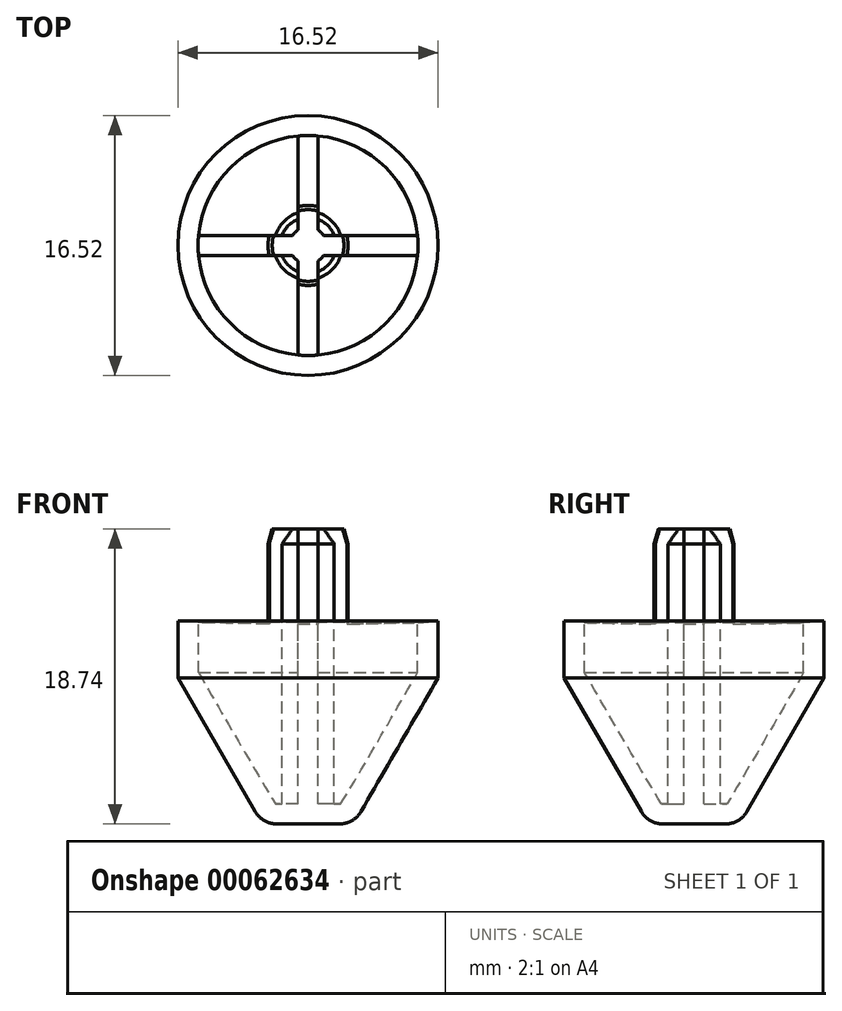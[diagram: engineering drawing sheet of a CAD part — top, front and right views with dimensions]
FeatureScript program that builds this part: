
annotation { "Feature Type Name" : "Feature", "Feature Type Description" : "" }
export const myFeature = defineFeature(function(context is Context, id is Id, definition is map)
    precondition{}
    {
        {
            var Q0;
            Q0=qCreatedBy(makeId("Front.planeOp"),FACE);
            var sketch = newSketch(context, id + "F0", { "sketchPlane" : qUnion([Q0])});
            skLineSegment(sketch, "E0.bottom", {"start": v(-2.54, 19.12) * mm, "end": v(2.54, 19.12) * mm});
            skLineSegment(sketch, "E0.top", {"start": v(-2.54, 15.94) * mm, "end": v(2.54, 15.94) * mm});
            skLineSegment(sketch, "E0.left", {"start": v(-2.54, 19.12) * mm, "end": v(-2.54, 15.94) * mm});
            skLineSegment(sketch, "E0.right", {"start": v(2.54, 19.12) * mm, "end": v(2.54, 15.94) * mm});
            skCircle(sketch, "E1", {"center": v(0, 10.12) * mm, "radius": 6.35 * mm, "construction": true});
            skLineSegment(sketch, "E2", {"start": v(0, 10.12) * mm, "end": v(0, 19.12) * mm, "construction": true});
            skLineSegment(sketch, "E3", {"start": v(-2.54, 15.94) * mm, "end": v(-8.26, 16.14) * mm});
            skLineSegment(sketch, "E4", {"start": v(0, 10.12) * mm, "end": v(0, 3.24) * mm, "construction": true});
            skLineSegment(sketch, "E5", {"start": v(-8.26, 16.14) * mm, "end": v(-8.26, 12.52) * mm});
            skLineSegment(sketch, "E6", {"start": v(-8.26, 12.52) * mm, "end": v(-2.9, 3.24) * mm});
            skLineSegment(sketch, "E7", {"start": v(-2.9, 3.24) * mm, "end": v(0, 3.24) * mm});
            skLineSegment(sketch, "E8", {"start": v(2.41, 20.39) * mm, "end": v(-2.41, 20.39) * mm});
            skLineSegment(sketch, "E9", {"start": v(0, 19.12) * mm, "end": v(0, 20.39) * mm});
            skArc(sketch, "E10", {"start": v(-2.41, 20.39) * mm, "mid": v(-2.62, 19.77) * mm, "end": v(-2.54, 19.12) * mm});
            skArc(sketch, "E11", {"start": v(2.54, 19.12) * mm, "mid": v(2.62, 19.77) * mm, "end": v(2.41, 20.39) * mm});
            skSolve(sketch);
        }
        {
            var Q0;
            Q0=qCreatedBy(makeId("Front.planeOp"),FACE);
            var sketch = newSketch(context, id + "F1", { "sketchPlane" : qUnion([Q0])});
            skLineSegment(sketch, "E12.0", {"start": v(-8.26, 16.14) * mm, "end": v(-8.26, 12.52) * mm});
            skLineSegment(sketch, "E13.0", {"start": v(-8.26, 12.52) * mm, "end": v(-2.9, 3.24) * mm});
            skLineSegment(sketch, "E14.0", {"start": v(-2.9, 3.24) * mm, "end": v(0, 3.24) * mm});
            skPoint(sketch, "E15.orphan", {"position": v(2.54, 19.12) * mm});
            skPoint(sketch, "E16.orphan", {"position": v(-2.54, 19.12) * mm});
            skLineSegment(sketch, "E17", {"start": v(0, 20.39) * mm, "end": v(0, 3.24) * mm});
            skPoint(sketch, "E18.orphan", {"position": v(2.41, 20.39) * mm});
            skPoint(sketch, "E19.0.end.orphan", {"position": v(-2.41, 20.39) * mm});
            skLineSegment(sketch, "E20", {"start": v(-1.02, 20.39) * mm, "end": v(0, 20.39) * mm});
            skLineSegment(sketch, "E21.0", {"start": v(-6.99, 12.86) * mm, "end": v(-2.17, 4.51) * mm});
            skLineSegment(sketch, "E21.1", {"start": v(-6.99, 16.03) * mm, "end": v(-6.99, 12.86) * mm});
            skLineSegment(sketch, "E22", {"start": v(-1.78, 19.12) * mm, "end": v(-1.78, 4.51) * mm});
            skLineSegment(sketch, "E23", {"start": v(-1.78, 4.51) * mm, "end": v(-2.17, 4.51) * mm});
            skPoint(sketch, "E24.orphan", {"position": v(-2.56, 4.51) * mm});
            skLineSegment(sketch, "E25", {"start": v(-1.78, 19.12) * mm, "end": v(-1.02, 20.39) * mm});
            skLineSegment(sketch, "E26", {"start": v(-8.26, 16.14) * mm, "end": v(-6.99, 16.03) * mm});
            skSolve(sketch);
        }
        {
            var Q0;
            Q0 = qSketchRegion(id + "F1", true);
            var Q1;
            Q1=sQuery(id+"F1.wireOp",EDGE,"E17");
            revolve(context, id + "F2", {"entities" : qUnion([Q0]), "axis" : qUnion([Q1]), "revolveType" : RevolveType.FULL});
        }
        {
            var Q0;
            Q0=makeQuery(id+"F2.opRevolve","SWEPT_FACE",FACE,{"disambiguationData":[OSD([sQuery(id+"F1.wireOp",EDGE,"E20")])]});
            var sketch = newSketch(context, id + "F3", { "sketchPlane" : qUnion([Q0])});
            skLineSegment(sketch, "E27.bottom", {"start": v(-7.62, 0.64) * mm, "end": v(7.62, 0.63) * mm});
            skLineSegment(sketch, "E27.top", {"start": v(-7.62, -0.63) * mm, "end": v(7.62, -0.64) * mm});
            skLineSegment(sketch, "E27.left", {"start": v(-7.62, 0.63) * mm, "end": v(-7.62, -0.63) * mm});
            skLineSegment(sketch, "E27.right", {"start": v(7.62, 0.63) * mm, "end": v(7.62, -0.63) * mm});
            skLineSegment(sketch, "E28", {"start": v(7.62, 0) * mm, "end": v(0, 0) * mm, "construction": true});
            skLineSegment(sketch, "E29", {"start": v(0, 0) * mm, "end": v(0, 0.64) * mm, "construction": true});
            skLineSegment(sketch, "E30.bottom", {"start": v(-0.63, 8.2) * mm, "end": v(0.63, 8.2) * mm});
            skLineSegment(sketch, "E30.top", {"start": v(-0.64, -8.32) * mm, "end": v(0.64, -8.32) * mm});
            skLineSegment(sketch, "E30.left", {"start": v(-0.63, 8.2) * mm, "end": v(-0.64, -8.32) * mm});
            skLineSegment(sketch, "E30.right", {"start": v(0.64, 8.2) * mm, "end": v(0.63, -8.32) * mm});
            skLineSegment(sketch, "E31", {"start": v(0, -8.32) * mm, "end": v(0, 0) * mm, "construction": true});
            skSolve(sketch);
        }
        {
            var Q0;
            {var subQ1=makeQuery(id+"F2.opRevolve","SWEPT_EDGE",EDGE,{"disambiguationData":[OSD([sQuery(id+"F1.wireOp",EDGE,"E20"),sQuery(id+"F1.wireOp",EDGE,"E25")])]});var subQ10=sQuery(id+"F3.wireOp",EDGE,"E27.bottom");var subQ11=makeQuery(id+"F3.imprint","INTERSECT",VERTEX,{"disambiguationData":[OD(0.0)],"derivedFrom":[subQ1,subQ10]});Q0=makeQuery(id+"F3.imprint","IMPRINT",FACE,{"disambiguationData":[TD([[makeQuery(id+"F3.imprint","IMPRINT",EDGE,{"disambiguationData":[TD([[subQ11,-1.0]])],"derivedFrom":subQ10}),-1.0]])]});}
            var sketch = newSketch(context, id + "F4", { "sketchPlane" : qUnion([Q0])});
            skLineSegment(sketch, "E32.0", {"start": v(0.64, 8.2) * mm, "end": v(0.63, 0.64) * mm});
            skLineSegment(sketch, "E33.0", {"start": v(-0.64, 8.2) * mm, "end": v(-0.64, 0.64) * mm});
            skLineSegment(sketch, "E34.0", {"start": v(-7.62, 0.64) * mm, "end": v(-0.64, 0.64) * mm});
            skLineSegment(sketch, "E35.0", {"start": v(-7.62, -0.63) * mm, "end": v(-0.64, -0.63) * mm});
            skLineSegment(sketch, "E36.0", {"start": v(7.62, 0.63) * mm, "end": v(7.62, -0.63) * mm});
            skLineSegment(sketch, "E37.0", {"start": v(-7.62, 0.63) * mm, "end": v(-7.62, -0.63) * mm});
            skLineSegment(sketch, "E38.0", {"start": v(-0.64, 8.2) * mm, "end": v(0.63, 8.2) * mm});
            skLineSegment(sketch, "E39.0", {"start": v(-0.64, -8.32) * mm, "end": v(0.64, -8.32) * mm});
            skLineSegment(sketch, "E40.trimOffspring", {"start": v(0.63, 0.64) * mm, "end": v(7.62, 0.63) * mm});
            skLineSegment(sketch, "E41.trimOffspring", {"start": v(-0.64, -0.63) * mm, "end": v(-0.64, -8.32) * mm});
            skLineSegment(sketch, "E42.trimOffspring", {"start": v(0.63, -0.64) * mm, "end": v(0.63, -8.32) * mm});
            skLineSegment(sketch, "E43.trimOffspring", {"start": v(0.63, -0.64) * mm, "end": v(7.62, -0.64) * mm});
            skSolve(sketch);
        }
        {
            var Q0;
            Q0 = qSketchRegion(id + "F4", true);
            var Q1;
            Q1=makeQuery(id+"F2.opRevolve","SWEPT_FACE",FACE,{"disambiguationData":[OSD([sQuery(id+"F1.wireOp",EDGE,"E21.0")])]});
            extrude(context, id + "F5", {"entities" : qUnion([Q0]), "operationType" : NewBodyOperationType.ADD, "endBound" : BoundingType.UP_TO_SURFACE, "oppositeDirection" : true, "endBoundEntityFace" : qUnion([Q1]), "depth" : 25.4 * mm, "hasSecondDirection" : true, "secondDirectionOppositeDirection" : false, "secondDirectionDepth" : 1.59 * mm});
        }
        {
            var Q0;
            Q0=qCreatedBy(makeId("Front.planeOp"),FACE);
            var sketch = newSketch(context, id + "F6", { "sketchPlane" : qUnion([Q0])});
            skLineSegment(sketch, "E44", {"start": v(-8.26, 16.14) * mm, "end": v(-8.26, 3.25) * mm});
            skLineSegment(sketch, "E45", {"start": v(-8.26, 3.25) * mm, "end": v(0, 3.25) * mm});
            skLineSegment(sketch, "E46", {"start": v(0, 3.25) * mm, "end": v(0, -0.35) * mm});
            skLineSegment(sketch, "E47", {"start": v(0, -0.35) * mm, "end": v(-10.78, -0.35) * mm});
            skLineSegment(sketch, "E48", {"start": v(-10.78, -0.35) * mm, "end": v(-10.78, 22.86) * mm});
            skLineSegment(sketch, "E49", {"start": v(-10.78, 22.86) * mm, "end": v(-2.03, 22.86) * mm});
            skPoint(sketch, "E50.orphan", {"position": v(8.26, 16.14) * mm});
            skLineSegment(sketch, "E51.0", {"start": v(-2.54, 21.03) * mm, "end": v(-2.54, 15.94) * mm});
            skPoint(sketch, "E52.orphan", {"position": v(-2.54, 15.94) * mm});
            skLineSegment(sketch, "E53", {"start": v(-2.54, 21.03) * mm, "end": v(-2.03, 22.86) * mm});
            skLineSegment(sketch, "E54.0", {"start": v(-8.26, 16.14) * mm, "end": v(-6.99, 16.03) * mm});
            skLineSegment(sketch, "E55", {"start": v(-6.99, 16.03) * mm, "end": v(-2.54, 15.94) * mm});
            skSolve(sketch);
        }
        {
            var Q0;
            Q0 = qSketchRegion(id + "F6", true);
            var Q1;
            Q1=sQuery(id+"F6.wireOp",EDGE,"E46");
            revolve(context, id + "F7", {"operationType" : NewBodyOperationType.REMOVE, "entities" : qUnion([Q0]), "axis" : qUnion([Q1]), "revolveType" : RevolveType.FULL, "oppositeDirection" : true});
        }
        {
            var Q0;
            Q0=makeQuery(id+"F2.opRevolve","SWEPT_EDGE",EDGE,{"disambiguationData":[OSD([sQuery(id+"F1.wireOp",EDGE,"E13.0"),sQuery(id+"F1.wireOp",EDGE,"E14.0")])]});
            fillet(context, id + "F8", {"entities" : qUnion([Q0]), "radius" : 1.59 * mm, "tangentPropagation" : true, "allowEdgeOverflow" : false});
        }
        {
            var Q0;
            Q0=qCreatedBy(makeId("Front.planeOp"),FACE);
            var sketch = newSketch(context, id + "F9", { "sketchPlane" : qUnion([Q0])});
            skLineSegment(sketch, "E56.bottom", {"start": v(-1.78, 18.88) * mm, "end": v(0, 18.88) * mm});
            skLineSegment(sketch, "E56.top", {"start": v(-1.17, 21.98) * mm, "end": v(0, 21.98) * mm});
            skLineSegment(sketch, "E56.left", {"start": v(-1.78, 18.88) * mm, "end": v(-1.78, 21.03) * mm});
            skLineSegment(sketch, "E56.right", {"start": v(0, 18.88) * mm, "end": v(0, 21.98) * mm});
            skLineSegment(sketch, "E57", {"start": v(-1.17, 21.98) * mm, "end": v(-1.78, 21.03) * mm});
            skPoint(sketch, "E58.orphan", {"position": v(-1.78, 21.98) * mm});
            skSolve(sketch);
        }
        {
            var Q0;
            Q0 = qSketchRegion(id + "F9", true);
            var Q1;
            Q1=sQuery(id+"F9.wireOp",EDGE,"E56.right");
            revolve(context, id + "F10", {"operationType" : NewBodyOperationType.ADD, "entities" : qUnion([Q0]), "axis" : qUnion([Q1]), "revolveType" : RevolveType.FULL});
        }
    });
